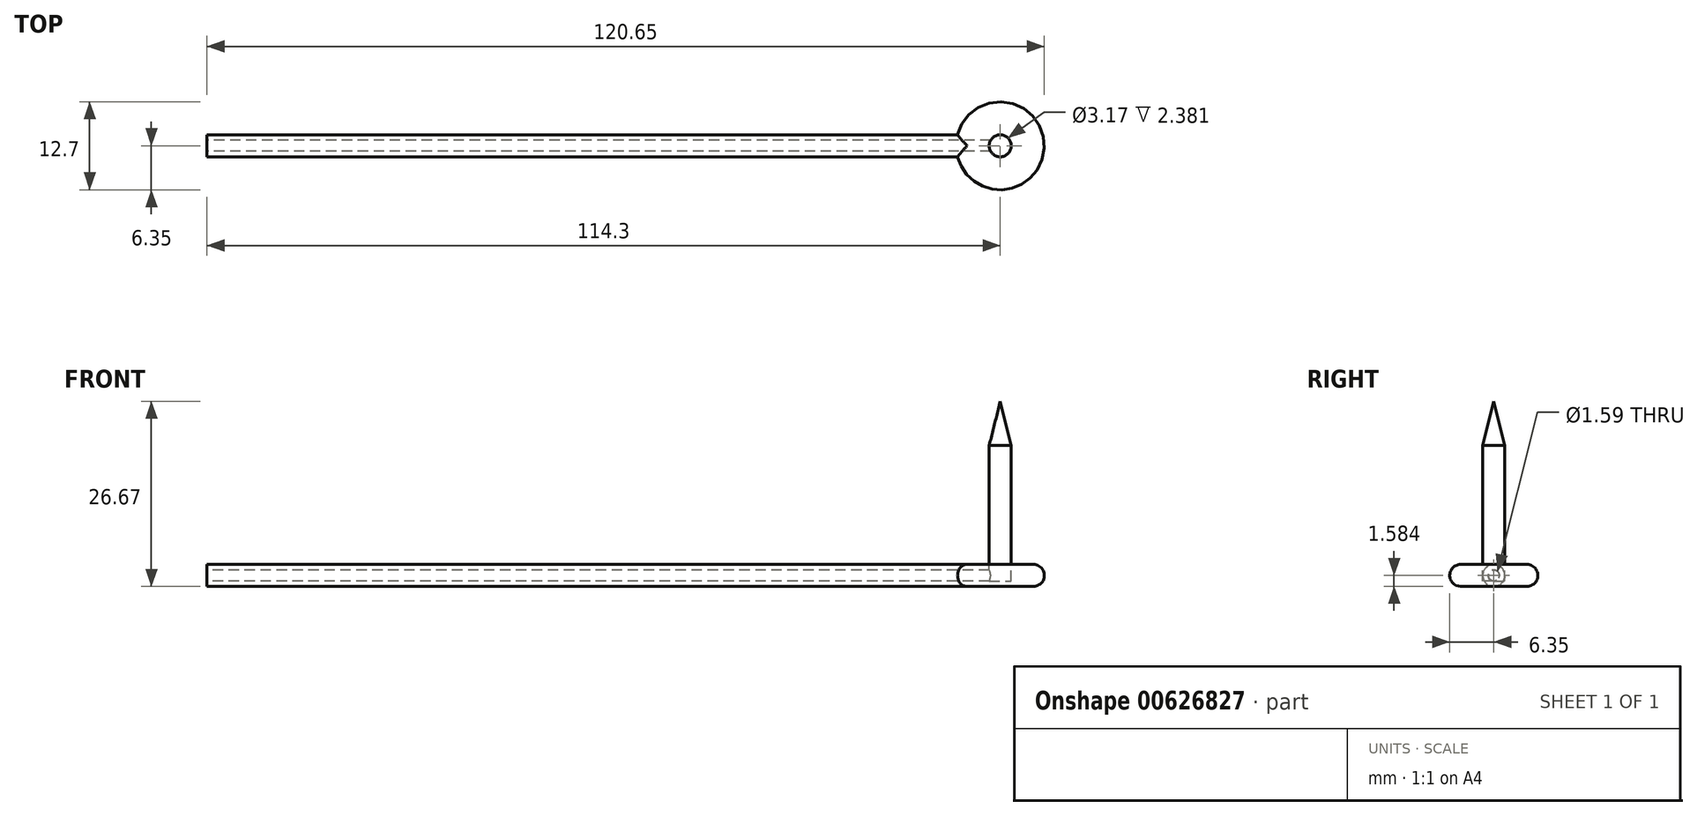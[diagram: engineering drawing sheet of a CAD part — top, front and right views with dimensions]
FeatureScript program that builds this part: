
annotation { "Feature Type Name" : "Feature", "Feature Type Description" : "" }
export const myFeature = defineFeature(function(context is Context, id is Id, definition is map)
    precondition{}
    {
        {
            var Q0;
            Q0=qCreatedBy(makeId("Front.planeOp"),FACE);
            var sketch = newSketch(context, id + "F0", { "sketchPlane" : qUnion([Q0])});
            skLineSegment(sketch, "E0.bottom", {"start": v(0, 0) * mm, "end": v(1.59, 0) * mm});
            skLineSegment(sketch, "E0.top", {"start": v(0, 19.53) * mm, "end": v(1.59, 19.53) * mm});
            skLineSegment(sketch, "E0.left", {"start": v(0, 0) * mm, "end": v(0, 19.53) * mm});
            skLineSegment(sketch, "E0.right", {"start": v(1.59, 0) * mm, "end": v(1.59, 19.53) * mm});
            skLineSegment(sketch, "E1", {"start": v(0, 19.53) * mm, "end": v(0, 25.88) * mm});
            skLineSegment(sketch, "E2", {"start": v(0, 25.88) * mm, "end": v(1.59, 19.53) * mm});
            skLineSegment(sketch, "E3", {"start": v(0, 0.48) * mm, "end": v(4.91, 0.48) * mm, "construction": true});
            skSolve(sketch);
        }
        {
            var Q0;
            Q0=makeQuery(id+"F0.imprint","IMPRINT",FACE,{"disambiguationData":[TD([[makeQuery(id+"F0.imprint","IMPRINT",EDGE,{"derivedFrom":sQuery(id+"F0.wireOp",EDGE,"E0.bottom")}),1.0]])]});
            var Q1;
            Q1=makeQuery(id+"F0.imprint","IMPRINT",FACE,{"disambiguationData":[TD([[makeQuery(id+"F0.imprint","IMPRINT",EDGE,{"derivedFrom":sQuery(id+"F0.wireOp",EDGE,"E0.top")}),1.0]])]});
            var Q2;
            Q2=sQuery(id+"F0.wireOp",EDGE,"E0.left");
            revolve(context, id + "F1", {"entities" : qUnion([Q0, Q1]), "axis" : qUnion([Q2]), "revolveType" : RevolveType.FULL});
        }
        {
            var Q0;
            Q0=qCreatedBy(makeId("Front.planeOp"),FACE);
            var sketch = newSketch(context, id + "F2", { "sketchPlane" : qUnion([Q0])});
            skLineSegment(sketch, "E4", {"start": v(-1.59, 0) * mm, "end": v(-1.59, 19.05) * mm});
            skLineSegment(sketch, "E5", {"start": v(1.59, 19.05) * mm, "end": v(1.59, 0) * mm});
            skLineSegment(sketch, "E6.bottom", {"start": v(0, 0) * mm, "end": v(-127, 0) * mm});
            skLineSegment(sketch, "E6.top", {"start": v(0, 0.8) * mm, "end": v(-127, 0.8) * mm});
            skLineSegment(sketch, "E6.left", {"start": v(0, 0.8) * mm, "end": v(0, 0) * mm});
            skLineSegment(sketch, "E6.right", {"start": v(-127, 0.8) * mm, "end": v(-127, 0) * mm});
            skSolve(sketch);
        }
        {
            var Q0;
            {var subQ5=sQuery(id+"F2.wireOp",EDGE,"E6.right");Q0=makeQuery(id+"F2.imprint","IMPRINT",FACE,{"disambiguationData":[TD([[makeQuery(id+"F2.imprint","IMPRINT",EDGE,{"derivedFrom":subQ5}),1.0]])]});}
            var Q1;
            Q1=sQuery(id+"F2.wireOp",EDGE,"E6.top");
            revolve(context, id + "F3", {"entities" : qUnion([Q0]), "axis" : qUnion([Q1]), "revolveType" : RevolveType.FULL});
        }
        {
            var Q0;
            Q0=qCreatedBy(makeId("Top.planeOp"),FACE);
            var sketch = newSketch(context, id + "F4", { "sketchPlane" : qUnion([Q0])});
            skCircle(sketch, "E7", {"center": v(0, 0) * mm, "radius": 6.35 * mm});
            skLineSegment(sketch, "E8.bottom", {"start": v(0, 1.59) * mm, "end": v(-114.3, 1.59) * mm});
            skLineSegment(sketch, "E8.top", {"start": v(0, -1.59) * mm, "end": v(-114.3, -1.59) * mm});
            skLineSegment(sketch, "E8.left", {"start": v(0, 1.59) * mm, "end": v(0, -1.59) * mm});
            skLineSegment(sketch, "E8.right", {"start": v(-114.3, 1.59) * mm, "end": v(-114.3, -1.59) * mm});
            skSolve(sketch);
        }
        {
            var Q0;
            {var subQ5=sQuery(id+"F4.wireOp",EDGE,"E8.left");Q0=makeQuery(id+"F4.imprint","IMPRINT",FACE,{"disambiguationData":[TD([[makeQuery(id+"F4.imprint","IMPRINT",EDGE,{"derivedFrom":subQ5}),1.0]])]});}
            var Q1;
            {var subQ5=sQuery(id+"F4.wireOp",EDGE,"E8.right");Q1=makeQuery(id+"F4.imprint","IMPRINT",FACE,{"disambiguationData":[TD([[makeQuery(id+"F4.imprint","IMPRINT",EDGE,{"derivedFrom":subQ5}),1.0]])]});}
            var Q2;
            {var subQ5=sQuery(id+"F4.wireOp",EDGE,"E8.left");Q2=makeQuery(id+"F4.imprint","IMPRINT",FACE,{"disambiguationData":[TD([[makeQuery(id+"F4.imprint","IMPRINT",EDGE,{"derivedFrom":subQ5}),-1.0]])]});}
            extrude(context, id + "F5", {"entities" : qUnion([Q0, Q1, Q2]), "depth" : 2.38 * mm, "offsetDistance" : 25.4 * mm, "hasSecondDirection" : true, "secondDirectionOppositeDirection" : true, "secondDirectionDepth" : 0.8 * mm});
        }
        {
            var Q0;
            Q0=makeQuery(id+"F5.opExtrude","CAP_EDGE",EDGE,{"disambiguationData":[OSD([sQuery(id+"F4.wireOp",EDGE,"E8.bottom")])],"isStart":false});
            var Q1;
            Q1=makeQuery(id+"F5.opExtrude","CAP_EDGE",EDGE,{"disambiguationData":[OSD([sQuery(id+"F4.wireOp",EDGE,"E8.top")])],"isStart":false});
            var Q2;
            Q2=makeQuery(id+"F5.opExtrude","CAP_EDGE",EDGE,{"disambiguationData":[OSD([sQuery(id+"F4.wireOp",EDGE,"E7")])],"isStart":false});
            var Q3;
            Q3=makeQuery(id+"F5.opExtrude","CAP_EDGE",EDGE,{"disambiguationData":[OSD([sQuery(id+"F4.wireOp",EDGE,"E7")])],"isStart":true});
            var Q4;
            Q4=makeQuery(id+"F5.opExtrude","CAP_EDGE",EDGE,{"disambiguationData":[OSD([sQuery(id+"F4.wireOp",EDGE,"E8.bottom")])],"isStart":true});
            var Q5;
            Q5=makeQuery(id+"F5.opExtrude","CAP_EDGE",EDGE,{"disambiguationData":[OSD([sQuery(id+"F4.wireOp",EDGE,"E8.top")])],"isStart":true});
            fillet(context, id + "F6", {"entities" : qUnion([Q0, Q1, Q2, Q3, Q4, Q5]), "radius" : 1.59 * mm, "tangentPropagation" : true, "allowEdgeOverflow" : false});
        }
        {
            var Q0;
            Q0=makeQuery(id+"F3.opRevolve","SWEPT_FACE",FACE,{"disambiguationData":[OSD([sQuery(id+"F2.wireOp",EDGE,"E6.right")])]});
            var sketch = newSketch(context, id + "F7", { "sketchPlane" : qUnion([Q0])});
            skLineSegment(sketch, "E9", {"start": v(0, 0) * mm, "end": v(0, 0) * mm});
            skCircle(sketch, "E10.0.0", {"center": v(0, 0.8) * mm, "radius": 0.8 * mm});
            skLineSegment(sketch, "E11", {"start": v(0, 0) * mm, "end": v(0, 1.59) * mm});
            skSolve(sketch);
        }
        {
            var Q0;
            {var subQ0=sQuery(id+"F7.wireOp",EDGE,"E11");Q0=makeQuery(id+"F7.imprint","IMPRINT",FACE,{"disambiguationData":[TD([[makeQuery(id+"F7.imprint","IMPRINT",EDGE,{"derivedFrom":subQ0}),-1.0]])]});}
            extrude(context, id + "F8", {"entities" : qUnion([Q0]), "operationType" : NewBodyOperationType.REMOVE, "oppositeDirection" : true, "depth" : 3.17 * mm, "offsetDistance" : 25.4 * mm});
        }
        {
            var Q0;
            Q0=makeQuery(id+"F3.opRevolve","SWEPT_FACE",FACE,{"disambiguationData":[OSD([sQuery(id+"F2.wireOp",EDGE,"E6.right")])]});
            var Q1;
            Q1=makeQuery(id+"F8.boolean.opBoolean","COPY",FACE,{"derivedFrom":makeQuery(id+"F8.opExtrude","CAP_FACE",FACE,{"disambiguationData":[OSD([sQuery(id+"F7.wireOp",EDGE,"E10.0.0"),sQuery(id+"F7.wireOp",EDGE,"E11")])],"isStart":false})});
            var Q2;
            Q2=makeQuery(id+"F1.opRevolve","SWEPT_BODY",BODY,{"disambiguationData":[OSD([sQuery(id+"F0.wireOp",EDGE,"E0.bottom"),sQuery(id+"F0.wireOp",EDGE,"E0.left"),sQuery(id+"F0.wireOp",EDGE,"E0.right"),sQuery(id+"F0.wireOp",EDGE,"E1"),sQuery(id+"F0.wireOp",EDGE,"E2")])]});
            extrude(context, id + "F9", {"entities" : qUnion([Q0, Q1]), "operationType" : NewBodyOperationType.REMOVE, "endBound" : BoundingType.UP_TO_BODY, "oppositeDirection" : true, "depth" : 25.4 * mm, "endBoundEntityBody" : qUnion([Q2]), "offsetDistance" : 25.4 * mm});
        }
        {
            var Q0;
            Q0=makeQuery(id+"F5.opExtrude","CAP_FACE",FACE,{"disambiguationData":[OSD([sQuery(id+"F4.wireOp",EDGE,"E7"),sQuery(id+"F4.wireOp",EDGE,"E8.bottom"),sQuery(id+"F4.wireOp",EDGE,"E8.top"),sQuery(id+"F4.wireOp",EDGE,"E8.right")])],"isStart":false});
            var sketch = newSketch(context, id + "F10", { "sketchPlane" : qUnion([Q0])});
            skCircle(sketch, "E12.0", {"center": v(0, 0) * mm, "radius": 1.59 * mm});
            skSolve(sketch);
        }
        {
            var Q0;
            Q0=makeQuery(id+"F10.imprint","IMPRINT",FACE,{"disambiguationData":[TD([[makeQuery(id+"F10.imprint","IMPRINT",EDGE,{"derivedFrom":sQuery(id+"F10.wireOp",EDGE,"E12.0")}),1.0]])]});
            var Q1;
            Q1=makeQuery(id+"F1.opRevolve","SWEPT_FACE",FACE,{"disambiguationData":[OSD([sQuery(id+"F0.wireOp",EDGE,"E0.bottom")])]});
            extrude(context, id + "F11", {"entities" : qUnion([Q0]), "operationType" : NewBodyOperationType.REMOVE, "endBound" : BoundingType.UP_TO_SURFACE, "oppositeDirection" : true, "depth" : 25.4 * mm, "endBoundEntityFace" : qUnion([Q1]), "offsetDistance" : 25.4 * mm});
        }
    });
